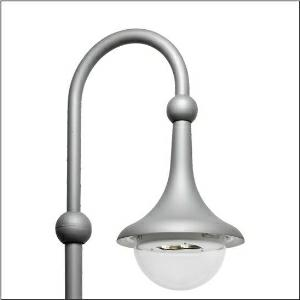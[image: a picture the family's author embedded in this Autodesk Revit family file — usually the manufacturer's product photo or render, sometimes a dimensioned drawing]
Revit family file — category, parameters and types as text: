
# Revit family: grosse_glocke___st1_2a_5xa1563e1b108_a6a2
name_source: partatom
category: Lighting Fixtures
units: mm (PartAtom-declared; Revit-internal decimal feet)

## family parameters
Cut with Voids When Loaded = No
Host = Face
Light Source = No
Part Type = Normal
Room Calculation Point = No
Round Connector Dimension = Use Diameter
Shared = No

## types (1)
- --- (1 x LED, 3150 lm, 23.4 W, 3000K)
    Apparent Load = 23 VA
    CIE Flux Codes = 29 66 95 99 100
    Color Rendering = 70
    Color Temperature = 3000K
    Default Elevation = 1800 mm
    Description = Large Bell, mast luminaire, primary light control with 3 zone facetted reflector, of plastic, silver coated, primary optical cover: enclosure, of PMMA, transparent, light distribution: ST1.2a, light emission: direct distribution, primary light characteristic: asymmetric, installation type: suspended mounting, LED, High Power LED, rated luminous flux: 3.150lm, luminous efficacy: 135lm/W, light colour: 730, colour temperature: 3000K, control gear: Plus, control: flexible luminous flux parameterisation, time-dependent luminous flux control, constant luminous flux control, digital communication interface, power reduction, electronic power reduction, mains connection: 230..240V, AC, 50/60Hz, start of lifetime: 23W, end of service life: 24W, reduction: 12W, luminaire housing, bell-shaped, of glass-fibre reinforced polyester, coated, Siteco® metallic grey (DB 702S), please order curved mast extension separately, diameter: 530mm, height: 695mm, mounting height: 4..6m, protection rating (complete): IP54, insulation class (complete): insulation class II (safety insulation), certification: CE, ENEC, VDE, impact resistance: IK08, standard-compliant lighting for roads and squares, packaging unit: 1 piece

Light Distribution: ST1.2a
    Height = 695 mm
    Lamp = 1 x LED
    Lamp Light Flux = 3150 lm
    Lamp Power = 23.4 W
    Lamp count = 1
    Length = 530 mm
    Luminous efficacy = 135 lm/W
    Manufacturer = Siteco
    ModVariant = No
    Model = 5XA1563E1B108
    Number of Poles = 1
    OnlyDefault = Yes
    Power Factor = 1
    Product Name = Große Glocke | ST1.2a
    Product group = mast luminaire | pylon annexe
    ProductGroupID = 6201
    Protection Class = Protection class II
    Protection Degree = IP 54
    RLX_Detail_Level = 1
    RLX_Emergency_Light_Flux = 0 lm
    RLX_Emergency_Type = 0
    RLX_Emergency_Type_DB = No
    RlxData = <blob elided: 52829 chars, md5=8042aa5a>
    Socket = socket
    Standby Power = 0 W
    System Light Flux = 3150 lm
    System Power = 23 W
    Type Comments = factory setting: luminous flux: 100 % | dim-lin: 254 | 460 mA
    Type Image = l_1347688.jpg
    URL = http://relux.com
    VarID = @adj_158988
    Voltage = 0 V
    Weight = 0.00 kg
    Width = 0 mm  [stored 0 ft]

note: [stored X ft] marks values corroborated as IEEE doubles in the binary element streams (Revit-internal decimal feet)

## geometry (parser evidence)
native form markers: Blend x4, Sweep x9
no freeform markers — native parametric forms only
